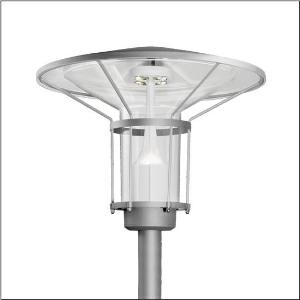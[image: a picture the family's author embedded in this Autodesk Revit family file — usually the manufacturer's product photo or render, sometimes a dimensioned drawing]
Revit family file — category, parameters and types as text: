
# Revit family: laterne_classic_iq___p1_0a_5xa5245lf14h_4a87
name_source: partatom
category: Lighting Fixtures
units: mm (PartAtom-declared; Revit-internal decimal feet)

## family parameters
Cut with Voids When Loaded = No
Host = Face
Light Source = No
Part Type = Normal
Room Calculation Point = No
Round Connector Dimension = Use Diameter
Shared = No

## types (1)
- --- (1 x LED, 1360 lm, 10 W, 4000K)
    Apparent Load = 10 VA
    CIE Flux Codes = 30 61 91 96 100
    Color Rendering = 70
    Color Temperature = 4000K
    Default Elevation = 1800 mm
    Description = Lantern Classic iQ, mast luminaire, Module 540 iQ-SR, primary light control with 3 zone facetted reflector, of plastic, silver coated, highly specular, structured, primary optical cover: cover, of PMMA, transparent, light distribution: P1.0a, light emission: direct distribution, primary light characteristic: strongly asymmetric, installation type: post-top, LED, High Power LED, rated luminous flux: 1.360lm, luminous efficacy: 136lm/W, light colour: 740, colour temperature: 4000K, control gear: ECG iQ, control: pre-setting: logarithmic dimming characteristic, Street-Remote, Auto-Match, Temp-Guard, Lumen-Switch, Night-Set, Smart-Wire, Light-Fading, Desk-Remote (wireless, voltage-free reading and setting of iQ features in the workshop via application-optimized NFC function/RFID function), optimised constant luminous flux control (CLO 2.0), with terminal, 6-pole, max. 2.5mm², mains connection: 230..240V, AC, 50/60Hz, start of lifetime: 10W, end of service life: 10W, reduction: 5W, luminaire housing, upper part, of glass-fibre reinforced polyester, coated, Siteco® metallic grey (DB 702S), diameter: 750mm, height: 596mm, spigot size: d x l = 76 x 70mm (post-top) | with reducer (optional accessory) 60 x 70mm, post-top mast mounting element, of diecast aluminium, coated, Siteco® metallic grey (DB 702S), Module 540 iQ-SR, traffic white (RAL 9016), equipment: standard, protection rating (complete): IP65, insulation class (complete): insulation class II (safety insulation), certification: CE, ENEC, VDE, packaging unit: 1 piece

Light Distribution: P1.0a
    Height = 596 mm
    Lamp = 1 x LED
    Lamp Light Flux = 1360 lm
    Lamp Power = 10 W
    Lamp count = 1
    Length = 750 mm
    Luminous efficacy = 136 lm/W
    Manufacturer = Siteco
    ModVariant = No
    Model = 5XA5245LF14H
    Number of Poles = 1
    OnlyDefault = Yes
    Power Factor = 1
    Product Name = Laterne Classic iQ | P1.0a
    Product group = mast luminaire | pylon top
    ProductGroupID = 6100
    Protection Class = Protection class II
    Protection Degree = IP 65
    RLX_Detail_Level = 1
    RLX_Emergency_Light_Flux = 0 lm
    RLX_Emergency_Type = 0
    RLX_Emergency_Type_DB = No
    RlxData = <blob elided: 98125 chars, md5=83aaba02>
    Socket = socket
    Standby Power = 0 W
    System Light Flux = 1360 lm
    System Power = 10 W
    Type Comments = factory setting: luminous flux: 100 % | dim-lin: 254 | 401 mA
    Type Image = l_1006052.jpg
    URL = http://relux.com
    VarID = @adj_130571
    Voltage = 0 V
    Weight = 0.00 kg
    Width = 0 mm  [stored 0 ft]

note: [stored X ft] marks values corroborated as IEEE doubles in the binary element streams (Revit-internal decimal feet)

## geometry (parser evidence)
native form markers: Blend x4, Sweep x9
no freeform markers — native parametric forms only
